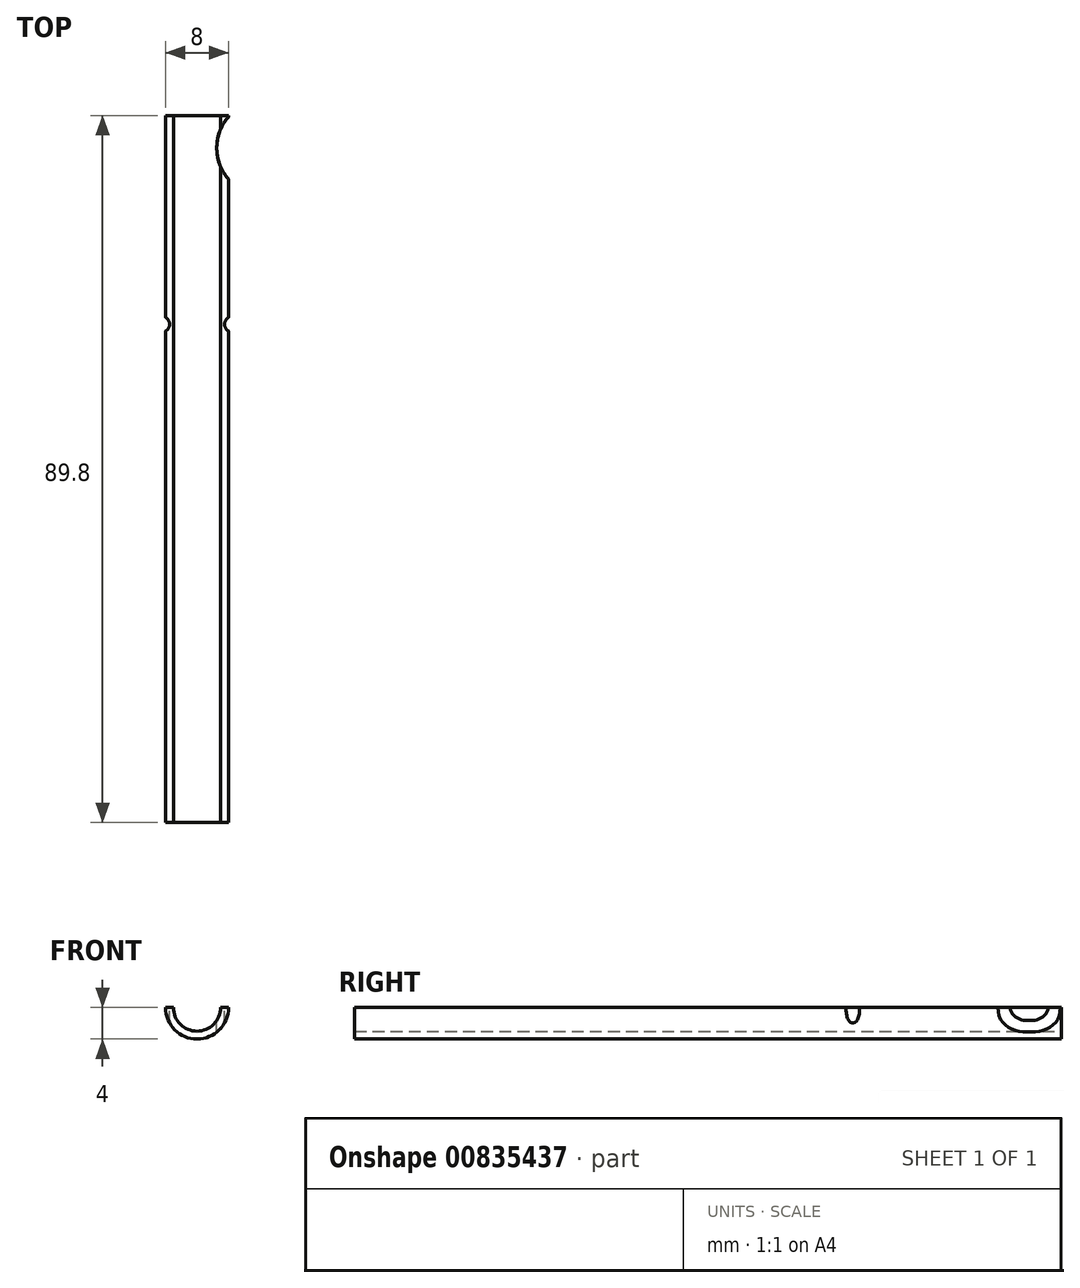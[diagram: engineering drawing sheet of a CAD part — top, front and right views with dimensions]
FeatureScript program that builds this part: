
annotation { "Feature Type Name" : "Feature", "Feature Type Description" : "" }
export const myFeature = defineFeature(function(context is Context, id is Id, definition is map)
    precondition{}
    {
        {
            var Q0;
            Q0=qCreatedBy(makeId("Front.planeOp"),FACE);
            var sketch = newSketch(context, id + "F0", { "sketchPlane" : qUnion([Q0])});
            skCircle(sketch, "E0", {"center": v(0, 0) * mm, "radius": 4 * mm});
            skCircle(sketch, "E1", {"center": v(0, 0) * mm, "radius": 3 * mm});
            skSolve(sketch);
        }
        {
            var Q0;
            Q0 = qSketchRegion(id + "F0", true);
            extrude(context, id + "F1", {"entities" : qUnion([Q0]), "depth" : 89.8 * mm, "offsetDistance" : 25 * mm});
        }
        {
            var Q0;
            Q0=makeQuery(id+"F1.opExtrude","CAP_FACE",FACE,{"disambiguationData":[OSD([sQuery(id+"F0.wireOp",EDGE,"E0"),sQuery(id+"F0.wireOp",EDGE,"E1")])],"isStart":false});
            var sketch = newSketch(context, id + "F2", { "sketchPlane" : qUnion([Q0])});
            skLineSegment(sketch, "E2", {"start": v(0, 0) * mm, "end": v(-5.92, 0) * mm});
            skLineSegment(sketch, "E3", {"start": v(0, 0) * mm, "end": v(6.08, 0) * mm});
            skLineSegment(sketch, "E4", {"start": v(-5.92, 0) * mm, "end": v(-5.92, 7.45) * mm});
            skLineSegment(sketch, "E5", {"start": v(-5.92, 7.45) * mm, "end": v(6.08, 7.45) * mm});
            skLineSegment(sketch, "E6", {"start": v(6.08, 7.45) * mm, "end": v(6.08, 0) * mm});
            skSolve(sketch);
        }
        {
            var Q0;
            Q0 = qSketchRegion(id + "F2", true);
            extrude(context, id + "F3", {"entities" : qUnion([Q0]), "operationType" : NewBodyOperationType.REMOVE, "oppositeDirection" : true, "depth" : 96.4 * mm, "offsetDistance" : 25 * mm});
        }
        {
            var Q0;
            Q0=qCreatedBy(makeId("Top.planeOp"),FACE);
            var sketch = newSketch(context, id + "F4", { "sketchPlane" : qUnion([Q0])});
            skCircle(sketch, "E7", {"center": v(8.5, -4.1) * mm, "radius": 6 * mm});
            skSolve(sketch);
        }
        {
            var Q0;
            Q0 = qSketchRegion(id + "F4", true);
            extrude(context, id + "F5", {"entities" : qUnion([Q0]), "operationType" : NewBodyOperationType.REMOVE, "oppositeDirection" : true, "depth" : 25 * mm, "offsetDistance" : 25 * mm, "hasSecondDirection" : true, "secondDirectionOppositeDirection" : false, "secondDirectionDepth" : 25 * mm});
        }
        {
            var Q0;
            {var subQ0=sQuery(id+"F0.wireOp",EDGE,"E0");var subQ1=sQuery(id+"F0.wireOp",EDGE,"E1");Q0=makeQuery(id+"F5.boolean.opBoolean","SPLIT",FACE,{"disambiguationData":[TD([makeQuery(id+"F1.opExtrude","CAP_FACE",FACE,{"disambiguationData":[OSD([subQ0,subQ1])],"isStart":false})])],"derivedFrom":makeQuery(id+"F3.boolean.opBoolean","COPY",FACE,{"disambiguationData":[OD(1.0)],"derivedFrom":makeQuery(id+"F3.opExtrude","SWEPT_FACE",FACE,{"disambiguationData":[OSD([sQuery(id+"F2.wireOp",EDGE,"E2"),sQuery(id+"F2.wireOp",EDGE,"E3")])]})})});}
            var sketch = newSketch(context, id + "F6", { "sketchPlane" : qUnion([Q0])});
            skCircle(sketch, "E8", {"center": v(4.5, -26.5) * mm, "radius": 1 * mm});
            skCircle(sketch, "E9", {"center": v(-4.5, -26.5) * mm, "radius": 1 * mm});
            skSolve(sketch);
        }
        {
            var Q0;
            Q0 = qSketchRegion(id + "F6", true);
            extrude(context, id + "F7", {"entities" : qUnion([Q0]), "operationType" : NewBodyOperationType.REMOVE, "oppositeDirection" : true, "depth" : 25 * mm, "offsetDistance" : 25 * mm, "hasSecondDirection" : true, "secondDirectionOppositeDirection" : false, "secondDirectionDepth" : 25 * mm});
        }
    });
